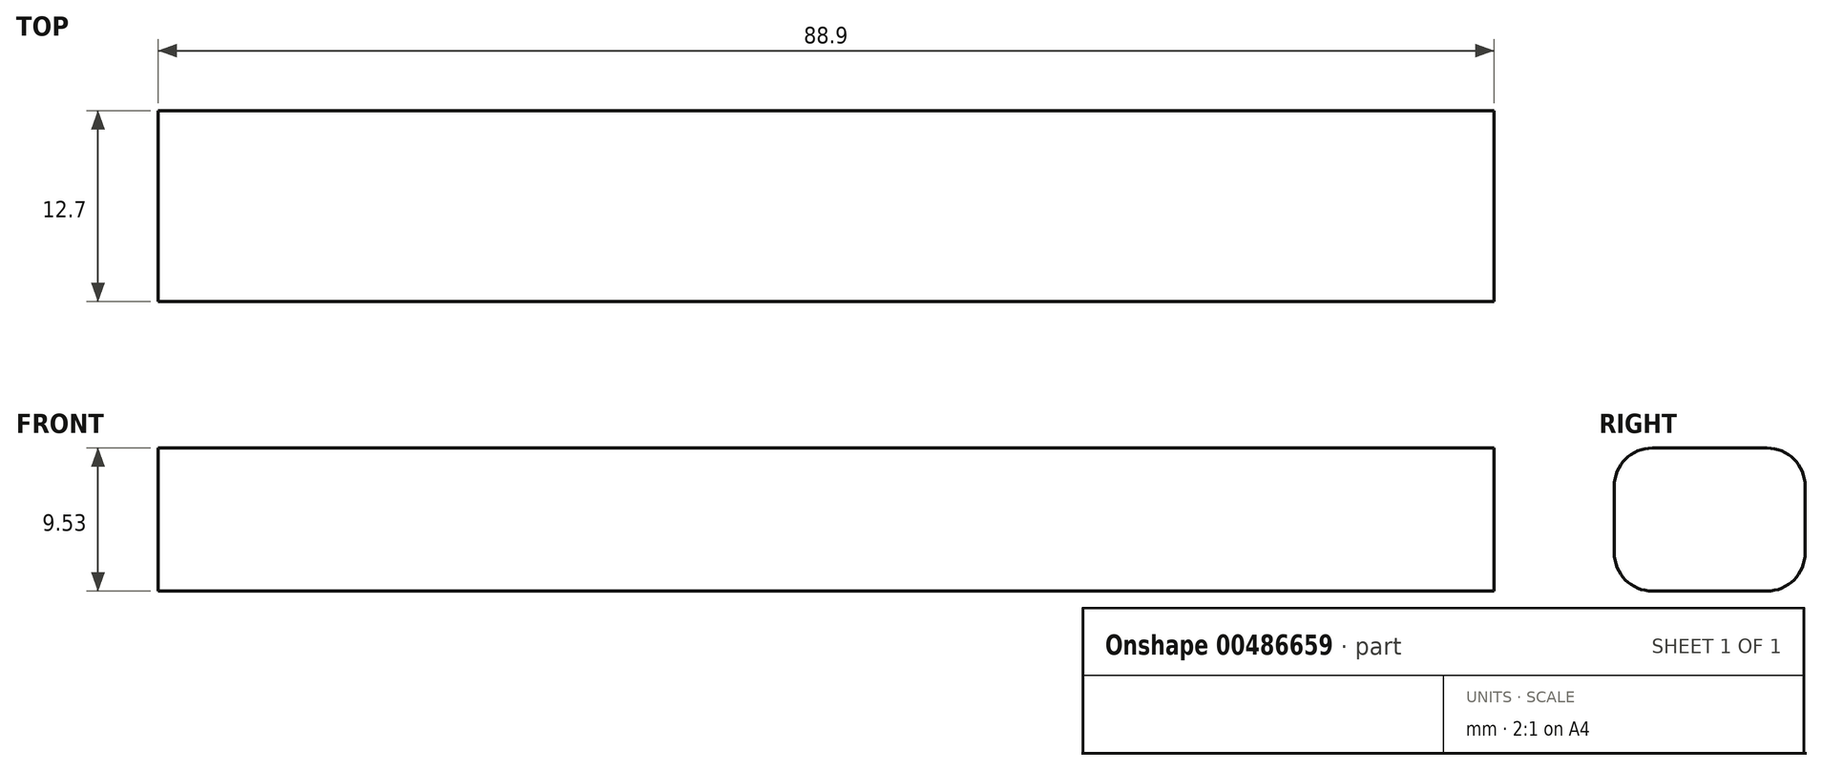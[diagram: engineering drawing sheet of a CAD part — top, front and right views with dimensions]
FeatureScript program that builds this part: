
annotation { "Feature Type Name" : "Feature", "Feature Type Description" : "" }
export const myFeature = defineFeature(function(context is Context, id is Id, definition is map)
    precondition{}
    {
        {
            var Q0;
            Q0=qCreatedBy(makeId("Top.planeOp"),FACE);
            var sketch = newSketch(context, id + "F0", { "sketchPlane" : qUnion([Q0])});
            skLineSegment(sketch, "E0.bottom", {"start": v(-44.45, 6.35) * mm, "end": v(44.45, 6.35) * mm});
            skLineSegment(sketch, "E0.top", {"start": v(-44.45, -6.35) * mm, "end": v(44.45, -6.35) * mm});
            skLineSegment(sketch, "E0.left", {"start": v(-44.45, 6.35) * mm, "end": v(-44.45, -6.35) * mm});
            skLineSegment(sketch, "E0.right", {"start": v(44.45, 6.35) * mm, "end": v(44.45, -6.35) * mm});
            skPoint(sketch, "E0.middle", {"position": v(0, 0) * mm});
            skSolve(sketch);
        }
        {
            var Q0;
            Q0 = qSketchRegion(id + "F0", true);
            extrude(context, id + "F1", {"entities" : qUnion([Q0]), "depth" : 9.52 * mm});
        }
        {
            var Q0;
            Q0=makeQuery(id+"F1.opExtrude","CAP_EDGE",EDGE,{"disambiguationData":[OSD([sQuery(id+"F0.wireOp",EDGE,"E0.bottom")])],"isStart":false});
            var Q1;
            Q1=makeQuery(id+"F1.opExtrude","CAP_EDGE",EDGE,{"disambiguationData":[OSD([sQuery(id+"F0.wireOp",EDGE,"E0.top")])],"isStart":false});
            var Q2;
            Q2=makeQuery(id+"F1.opExtrude","CAP_EDGE",EDGE,{"disambiguationData":[OSD([sQuery(id+"F0.wireOp",EDGE,"E0.top")])],"isStart":true});
            var Q3;
            Q3=makeQuery(id+"F1.opExtrude","CAP_EDGE",EDGE,{"disambiguationData":[OSD([sQuery(id+"F0.wireOp",EDGE,"E0.bottom")])],"isStart":true});
            fillet(context, id + "F2", {"entities" : qUnion([Q0, Q1, Q2, Q3]), "radius" : 2.54 * mm, "tangentPropagation" : true, "allowEdgeOverflow" : false});
        }
    });
